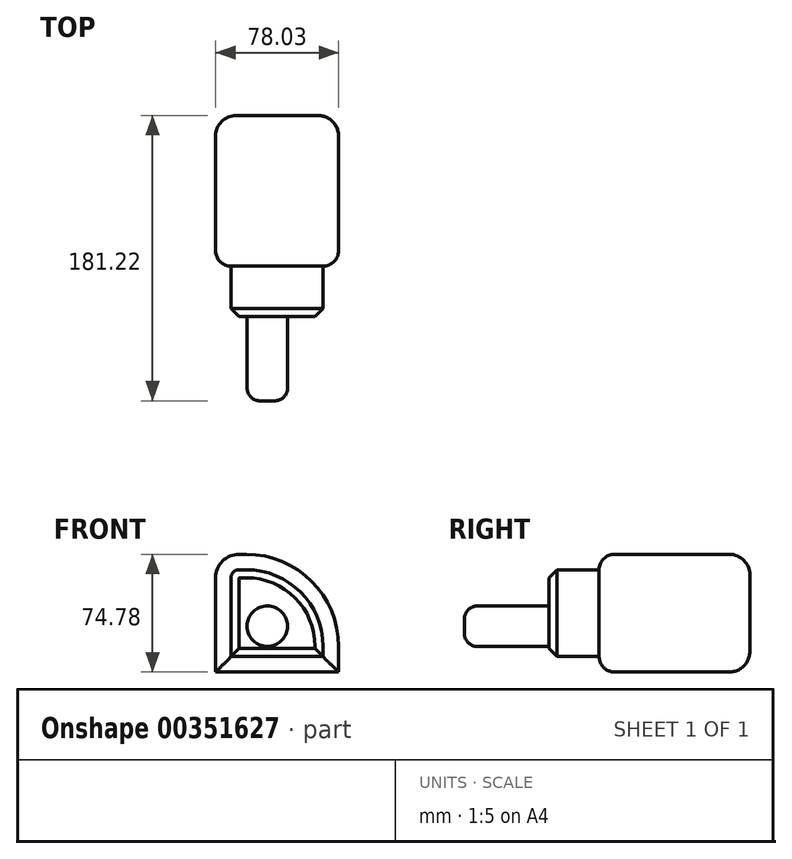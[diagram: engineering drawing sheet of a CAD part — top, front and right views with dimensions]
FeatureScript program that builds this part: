
annotation { "Feature Type Name" : "Feature", "Feature Type Description" : "" }
export const myFeature = defineFeature(function(context is Context, id is Id, definition is map)
    precondition{}
    {
        {
            var Q0;
            Q0=qCreatedBy(makeId("Front.planeOp"),FACE);
            var sketch = newSketch(context, id + "F0", { "sketchPlane" : qUnion([Q0])});
            skLineSegment(sketch, "E0.bottom", {"start": v(-32.86, -29.08) * mm, "end": v(45.17, -29.08) * mm});
            skLineSegment(sketch, "E0.top", {"start": v(-32.86, 45.7) * mm, "end": v(45.17, 45.7) * mm});
            skLineSegment(sketch, "E0.left", {"start": v(-32.86, -29.08) * mm, "end": v(-32.86, 45.7) * mm});
            skLineSegment(sketch, "E0.right", {"start": v(45.17, -29.08) * mm, "end": v(45.17, 45.7) * mm});
            skSolve(sketch);
        }
        {
            var Q0;
            Q0=makeQuery(id+"F0.imprint","IMPRINT",FACE,{"disambiguationData":[TD([[makeQuery(id+"F0.imprint","IMPRINT",EDGE,{"derivedFrom":sQuery(id+"F0.wireOp",EDGE,"E0.bottom")}),1.0]])]});
            extrude(context, id + "F1", {"entities" : qUnion([Q0]), "depth" : 95.69 * mm});
        }
        {
            var Q0;
            Q0=makeQuery(id+"F1.opExtrude","SWEPT_EDGE",EDGE,{"disambiguationData":[OSD([sQuery(id+"F0.wireOp",EDGE,"E0.top"),sQuery(id+"F0.wireOp",EDGE,"E0.right")])]});
            fillet(context, id + "F2", {"entities" : qUnion([Q0]), "radius" : 58.55 * mm, "tangentPropagation" : true, "allowEdgeOverflow" : false});
        }
        {
            var Q0;
            Q0=makeQuery(id+"F1.opExtrude","SWEPT_EDGE",EDGE,{"disambiguationData":[OSD([sQuery(id+"F0.wireOp",EDGE,"E0.top"),sQuery(id+"F0.wireOp",EDGE,"E0.left")])]});
            fillet(context, id + "F3", {"entities" : qUnion([Q0]), "radius" : 14.9 * mm, "tangentPropagation" : true, "allowEdgeOverflow" : false});
        }
        {
            var Q0;
            Q0=makeQuery(id+"F1.opExtrude","CAP_FACE",FACE,{"disambiguationData":[OSD([sQuery(id+"F0.wireOp",EDGE,"E0.bottom"),sQuery(id+"F0.wireOp",EDGE,"E0.top"),sQuery(id+"F0.wireOp",EDGE,"E0.left"),sQuery(id+"F0.wireOp",EDGE,"E0.right")])],"isStart":false});
            fillet(context, id + "F4", {"entities" : qUnion([Q0]), "radius" : 9.79 * mm, "tangentPropagation" : true, "allowEdgeOverflow" : false});
        }
        {
            var Q0;
            {var subQ0=sQuery(id+"F0.wireOp",EDGE,"E0.right");var subQ1=sQuery(id+"F0.wireOp",EDGE,"E0.top");Q0=makeQuery(id+"F2.opFillet","BLEND_EDGE",EDGE,{"blendedFrom":[makeQuery(id+"F1.opExtrude","SWEPT_EDGE",EDGE,{"disambiguationData":[OSD([subQ1,subQ0])]}),makeQuery(id+"F1.opExtrude","CAP_FACE",FACE,{"disambiguationData":[OSD([sQuery(id+"F0.wireOp",EDGE,"E0.bottom"),subQ1,sQuery(id+"F0.wireOp",EDGE,"E0.left"),subQ0])],"isStart":true})],"blendedInto":[makeQuery(id+"F1.opExtrude","CAP_FACE",FACE,{"disambiguationData":[OSD([sQuery(id+"F0.wireOp",EDGE,"E0.bottom"),subQ1,sQuery(id+"F0.wireOp",EDGE,"E0.left"),subQ0])],"isStart":true})]});}
            var Q1;
            Q1=makeQuery(id+"F1.opExtrude","CAP_FACE",FACE,{"disambiguationData":[OSD([sQuery(id+"F0.wireOp",EDGE,"E0.bottom"),sQuery(id+"F0.wireOp",EDGE,"E0.top"),sQuery(id+"F0.wireOp",EDGE,"E0.left"),sQuery(id+"F0.wireOp",EDGE,"E0.right")])],"isStart":true});
            fillet(context, id + "F5", {"entities" : qUnion([Q0, Q1]), "radius" : 12.96 * mm, "tangentPropagation" : true, "allowEdgeOverflow" : false});
        }
        {
            var Q0;
            Q0=makeQuery(id+"F1.opExtrude","CAP_FACE",FACE,{"disambiguationData":[OSD([sQuery(id+"F0.wireOp",EDGE,"E0.bottom"),sQuery(id+"F0.wireOp",EDGE,"E0.top"),sQuery(id+"F0.wireOp",EDGE,"E0.left"),sQuery(id+"F0.wireOp",EDGE,"E0.right")])],"isStart":false});
            extrude(context, id + "F6", {"entities" : qUnion([Q0]), "operationType" : NewBodyOperationType.ADD, "depth" : 31.88 * mm});
        }
        {
            var Q0;
            Q0=makeQuery(id+"F6.opExtrude","CAP_FACE",FACE,{"disambiguationData":[OSD([sQuery(id+"F0.wireOp",EDGE,"E0.bottom"),sQuery(id+"F0.wireOp",EDGE,"E0.top"),sQuery(id+"F0.wireOp",EDGE,"E0.left"),sQuery(id+"F0.wireOp",EDGE,"E0.right")])],"isStart":false});
            chamfer(context, id + "F7", {"entities" : qUnion([Q0]), "width" : 5.08 * mm, "tangentPropagation" : true});
        }
        {
            var Q0;
            Q0=makeQuery(id+"F6.opExtrude","CAP_FACE",FACE,{"disambiguationData":[OSD([sQuery(id+"F0.wireOp",EDGE,"E0.bottom"),sQuery(id+"F0.wireOp",EDGE,"E0.top"),sQuery(id+"F0.wireOp",EDGE,"E0.left"),sQuery(id+"F0.wireOp",EDGE,"E0.right")])],"isStart":false});
            var sketch = newSketch(context, id + "F8", { "sketchPlane" : qUnion([Q0])});
            skCircle(sketch, "E1", {"center": v(0, 0) * mm, "radius": 12.87 * mm});
            skSolve(sketch);
        }
        {
            var Q0;
            Q0=makeQuery(id+"F8.imprint","IMPRINT",FACE,{"disambiguationData":[TD([[makeQuery(id+"F8.imprint","IMPRINT",EDGE,{"derivedFrom":sQuery(id+"F8.wireOp",EDGE,"E1")}),1.0]])]});
            extrude(context, id + "F9", {"entities" : qUnion([Q0]), "operationType" : NewBodyOperationType.ADD, "depth" : 53.66 * mm});
        }
        {
            var Q0;
            Q0=makeQuery(id+"F9.opExtrude","CAP_EDGE",EDGE,{"disambiguationData":[OSD([sQuery(id+"F8.wireOp",EDGE,"E1")])],"isStart":false});
            fillet(context, id + "F10", {"entities" : qUnion([Q0]), "radius" : 8.17 * mm, "tangentPropagation" : true, "allowEdgeOverflow" : false});
        }
    });
